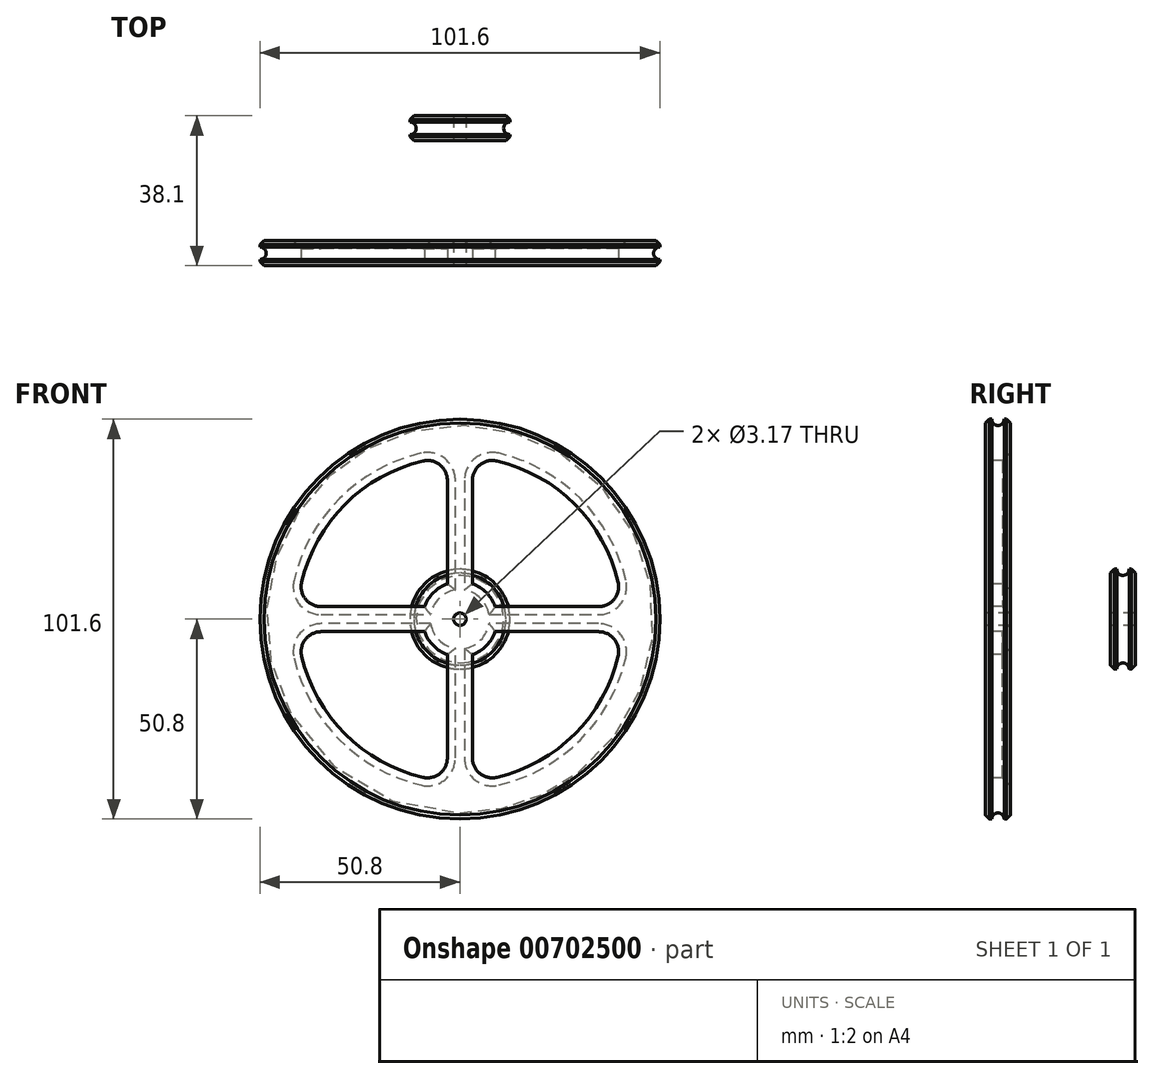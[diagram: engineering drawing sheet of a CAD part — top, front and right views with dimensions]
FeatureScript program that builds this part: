
annotation { "Feature Type Name" : "Feature", "Feature Type Description" : "" }
export const myFeature = defineFeature(function(context is Context, id is Id, definition is map)
    precondition{}
    {
        {
            var Q0;
            Q0=qCreatedBy(makeId("Right.planeOp"),FACE);
            var sketch = newSketch(context, id + "F0", { "sketchPlane" : qUnion([Q0])});
            skLineSegment(sketch, "E0", {"start": v(10.45, 0) * mm, "end": v(23.17, 0) * mm, "construction": true});
            skLineSegment(sketch, "E1", {"start": v(19.05, 1.59) * mm, "end": v(12.7, 1.59) * mm});
            skLineSegment(sketch, "E2", {"start": v(12.7, 1.59) * mm, "end": v(12.7, 12.7) * mm});
            skLineSegment(sketch, "E3", {"start": v(19.05, 1.59) * mm, "end": v(19.05, 12.7) * mm});
            skLineSegment(sketch, "E4", {"start": v(19.05, 12.7) * mm, "end": v(17.46, 12.7) * mm});
            skLineSegment(sketch, "E5", {"start": v(12.7, 12.7) * mm, "end": v(14.29, 12.7) * mm});
            skArc(sketch, "E6", {"start": v(14.29, 12.7) * mm, "mid": v(15.88, 11.11) * mm, "end": v(17.46, 12.7) * mm});
            skLineSegment(sketch, "E7", {"start": v(-12.7, 1.59) * mm, "end": v(-12.7, 50.8) * mm});
            skLineSegment(sketch, "E8", {"start": v(-12.7, 50.8) * mm, "end": v(-14.29, 50.8) * mm});
            skLineSegment(sketch, "E9", {"start": v(-12.7, 1.59) * mm, "end": v(-19.05, 1.59) * mm});
            skLineSegment(sketch, "E10", {"start": v(-19.05, 1.59) * mm, "end": v(-19.05, 50.8) * mm});
            skLineSegment(sketch, "E11", {"start": v(-19.05, 50.8) * mm, "end": v(-17.46, 50.8) * mm});
            skLineSegment(sketch, "E12", {"start": v(-3.92, 0) * mm, "end": v(-13.74, 0) * mm, "construction": true});
            skArc(sketch, "E13", {"start": v(-17.46, 50.8) * mm, "mid": v(-15.88, 49.21) * mm, "end": v(-14.29, 50.8) * mm});
            skSolve(sketch);
        }
        {
            var Q0;
            Q0=makeQuery(id+"F0.imprint","IMPRINT",FACE,{"disambiguationData":[TD([[makeQuery(id+"F0.imprint","IMPRINT",EDGE,{"derivedFrom":sQuery(id+"F0.wireOp",EDGE,"E1")}),-1.0]])]});
            var Q1;
            Q1=makeQuery(id+"F0.imprint","IMPRINT",FACE,{"disambiguationData":[TD([[makeQuery(id+"F0.imprint","IMPRINT",EDGE,{"derivedFrom":sQuery(id+"F0.wireOp",EDGE,"E7")}),1.0]])]});
            var Q2;
            Q2=sQuery(id+"F0.wireOp",EDGE,"E0");
            revolve(context, id + "F1", {"entities" : qUnion([Q0, Q1]), "axis" : qUnion([Q2]), "revolveType" : RevolveType.FULL});
        }
        {
            var Q0;
            Q0=makeQuery(id+"F1.opRevolve","SWEPT_EDGE",EDGE,{"disambiguationData":[OSD([sQuery(id+"F0.wireOp",EDGE,"E3"),sQuery(id+"F0.wireOp",EDGE,"E4")])]});
            var Q1;
            Q1=makeQuery(id+"F1.opRevolve","SWEPT_EDGE",EDGE,{"disambiguationData":[OSD([sQuery(id+"F0.wireOp",EDGE,"E2"),sQuery(id+"F0.wireOp",EDGE,"E5")])]});
            var Q2;
            Q2=makeQuery(id+"F1.opRevolve","SWEPT_EDGE",EDGE,{"disambiguationData":[OSD([sQuery(id+"F0.wireOp",EDGE,"E7"),sQuery(id+"F0.wireOp",EDGE,"E8")])]});
            var Q3;
            Q3=makeQuery(id+"F1.opRevolve","SWEPT_EDGE",EDGE,{"disambiguationData":[OSD([sQuery(id+"F0.wireOp",EDGE,"E10"),sQuery(id+"F0.wireOp",EDGE,"E11")])]});
            chamfer(context, id + "F2", {"entities" : qUnion([Q0, Q1, Q2, Q3]), "width" : 1.02 * mm, "tangentPropagation" : true});
        }
        {
            var Q0;
            Q0=makeQuery(id+"F1.opRevolve","SWEPT_FACE",FACE,{"disambiguationData":[OSD([sQuery(id+"F0.wireOp",EDGE,"E10")])]});
            var sketch = newSketch(context, id + "F3", { "sketchPlane" : qUnion([Q0])});
            skArc(sketch, "E14", {"start": v(-3.17, 8.98) * mm, "mid": v(-6.74, 6.74) * mm, "end": v(-8.98, 3.18) * mm});
            skArc(sketch, "E15", {"start": v(-3.18, 41.15) * mm, "mid": v(-29.19, 29.19) * mm, "end": v(-41.15, 3.17) * mm});
            skLineSegment(sketch, "E16", {"start": v(-3.18, 41.15) * mm, "end": v(-3.17, 8.98) * mm});
            skLineSegment(sketch, "E17", {"start": v(3.18, 41.15) * mm, "end": v(3.18, 8.98) * mm});
            skLineSegment(sketch, "E18", {"start": v(8.98, 3.18) * mm, "end": v(41.15, 3.18) * mm});
            skLineSegment(sketch, "E19", {"start": v(8.98, -3.18) * mm, "end": v(41.15, -3.18) * mm});
            skLineSegment(sketch, "E20", {"start": v(3.17, -8.98) * mm, "end": v(3.18, -41.15) * mm});
            skLineSegment(sketch, "E21", {"start": v(-3.18, -8.98) * mm, "end": v(-3.18, -41.15) * mm});
            skLineSegment(sketch, "E22", {"start": v(-8.98, -3.17) * mm, "end": v(-41.15, -3.18) * mm});
            skLineSegment(sketch, "E23", {"start": v(-8.98, 3.18) * mm, "end": v(-41.15, 3.17) * mm});
            skArc(sketch, "E24.trimOffspring", {"start": v(41.15, 3.18) * mm, "mid": v(29.19, 29.19) * mm, "end": v(3.18, 41.15) * mm});
            skArc(sketch, "E25.trimOffspring", {"start": v(3.17, -41.15) * mm, "mid": v(29.19, -29.19) * mm, "end": v(41.15, -3.18) * mm});
            skArc(sketch, "E26.trimOffspring", {"start": v(-41.15, -3.18) * mm, "mid": v(-29.19, -29.19) * mm, "end": v(-3.18, -41.15) * mm});
            skArc(sketch, "E27.trimOffspring", {"start": v(8.98, 3.18) * mm, "mid": v(6.74, 6.74) * mm, "end": v(3.18, 8.98) * mm});
            skArc(sketch, "E28.trimOffspring", {"start": v(3.17, -8.98) * mm, "mid": v(6.74, -6.74) * mm, "end": v(8.98, -3.18) * mm});
            skArc(sketch, "E29.trimOffspring", {"start": v(-8.98, -3.18) * mm, "mid": v(-6.74, -6.74) * mm, "end": v(-3.18, -8.98) * mm});
            skSolve(sketch);
        }
        {
            var Q0;
            Q0=makeQuery(id+"F3.imprint","IMPRINT",FACE,{"disambiguationData":[TD([[makeQuery(id+"F3.imprint","IMPRINT",EDGE,{"derivedFrom":sQuery(id+"F3.wireOp",EDGE,"E14")}),-1.0]])]});
            var Q1;
            Q1=makeQuery(id+"F3.imprint","IMPRINT",FACE,{"disambiguationData":[TD([[makeQuery(id+"F3.imprint","IMPRINT",EDGE,{"derivedFrom":sQuery(id+"F3.wireOp",EDGE,"E17")}),1.0]])]});
            var Q2;
            Q2=makeQuery(id+"F3.imprint","IMPRINT",FACE,{"disambiguationData":[TD([[makeQuery(id+"F3.imprint","IMPRINT",EDGE,{"derivedFrom":sQuery(id+"F3.wireOp",EDGE,"E19")}),-1.0]])]});
            var Q3;
            Q3=makeQuery(id+"F3.imprint","IMPRINT",FACE,{"disambiguationData":[TD([[makeQuery(id+"F3.imprint","IMPRINT",EDGE,{"derivedFrom":sQuery(id+"F3.wireOp",EDGE,"E21")}),-1.0]])]});
            extrude(context, id + "F4", {"entities" : qUnion([Q0, Q1, Q2, Q3]), "operationType" : NewBodyOperationType.REMOVE, "oppositeDirection" : true, "depth" : 25.4 * mm, "offsetDistance" : 25.4 * mm});
        }
        {
            var Q0;
            Q0=makeQuery(id+"F4.boolean.opBoolean","COPY",EDGE,{"derivedFrom":makeQuery(id+"F4.opExtrude","SWEPT_EDGE",EDGE,{"disambiguationData":[OSD([sQuery(id+"F3.wireOp",EDGE,"E15"),sQuery(id+"F3.wireOp",EDGE,"E16")])]})});
            var Q1;
            Q1=makeQuery(id+"F4.boolean.opBoolean","COPY",EDGE,{"derivedFrom":makeQuery(id+"F4.opExtrude","SWEPT_EDGE",EDGE,{"disambiguationData":[OSD([sQuery(id+"F3.wireOp",EDGE,"E17"),sQuery(id+"F3.wireOp",EDGE,"E24.trimOffspring")])]})});
            var Q2;
            Q2=makeQuery(id+"F4.boolean.opBoolean","COPY",EDGE,{"derivedFrom":makeQuery(id+"F4.opExtrude","SWEPT_EDGE",EDGE,{"disambiguationData":[OSD([sQuery(id+"F3.wireOp",EDGE,"E18"),sQuery(id+"F3.wireOp",EDGE,"E24.trimOffspring")])]})});
            var Q3;
            Q3=makeQuery(id+"F4.boolean.opBoolean","COPY",EDGE,{"derivedFrom":makeQuery(id+"F4.opExtrude","SWEPT_EDGE",EDGE,{"disambiguationData":[OSD([sQuery(id+"F3.wireOp",EDGE,"E19"),sQuery(id+"F3.wireOp",EDGE,"E25.trimOffspring")])]})});
            var Q4;
            Q4=makeQuery(id+"F4.boolean.opBoolean","COPY",EDGE,{"derivedFrom":makeQuery(id+"F4.opExtrude","SWEPT_EDGE",EDGE,{"disambiguationData":[OSD([sQuery(id+"F3.wireOp",EDGE,"E20"),sQuery(id+"F3.wireOp",EDGE,"E25.trimOffspring")])]})});
            var Q5;
            Q5=makeQuery(id+"F4.boolean.opBoolean","COPY",EDGE,{"derivedFrom":makeQuery(id+"F4.opExtrude","SWEPT_EDGE",EDGE,{"disambiguationData":[OSD([sQuery(id+"F3.wireOp",EDGE,"E21"),sQuery(id+"F3.wireOp",EDGE,"E26.trimOffspring")])]})});
            var Q6;
            Q6=makeQuery(id+"F4.boolean.opBoolean","COPY",EDGE,{"derivedFrom":makeQuery(id+"F4.opExtrude","SWEPT_EDGE",EDGE,{"disambiguationData":[OSD([sQuery(id+"F3.wireOp",EDGE,"E22"),sQuery(id+"F3.wireOp",EDGE,"E26.trimOffspring")])]})});
            var Q7;
            Q7=makeQuery(id+"F4.boolean.opBoolean","COPY",EDGE,{"derivedFrom":makeQuery(id+"F4.opExtrude","SWEPT_EDGE",EDGE,{"disambiguationData":[OSD([sQuery(id+"F3.wireOp",EDGE,"E15"),sQuery(id+"F3.wireOp",EDGE,"E23")])]})});
            fillet(context, id + "F5", {"entities" : qUnion([Q0, Q1, Q2, Q3, Q4, Q5, Q6, Q7]), "radius" : 5.08 * mm, "tangentPropagation" : true, "allowEdgeOverflow" : false});
        }
        {
            var Q0;
            Q0=makeQuery(id+"F4.boolean.opBoolean","COPY",EDGE,{"derivedFrom":makeQuery(id+"F4.opExtrude","CAP_EDGE",EDGE,{"disambiguationData":[OSD([sQuery(id+"F3.wireOp",EDGE,"E22")])],"isStart":true})});
            var Q1;
            Q1=makeQuery(id+"F4.boolean.opBoolean","COPY",EDGE,{"derivedFrom":makeQuery(id+"F4.opExtrude","CAP_EDGE",EDGE,{"disambiguationData":[OSD([sQuery(id+"F3.wireOp",EDGE,"E15")])],"isStart":true})});
            var Q2;
            Q2=makeQuery(id+"F4.boolean.opBoolean","COPY",EDGE,{"derivedFrom":makeQuery(id+"F4.opExtrude","CAP_EDGE",EDGE,{"disambiguationData":[OSD([sQuery(id+"F3.wireOp",EDGE,"E24.trimOffspring")])],"isStart":true})});
            var Q3;
            Q3=makeQuery(id+"F4.boolean.opBoolean","COPY",EDGE,{"derivedFrom":makeQuery(id+"F4.opExtrude","CAP_EDGE",EDGE,{"disambiguationData":[OSD([sQuery(id+"F3.wireOp",EDGE,"E25.trimOffspring")])],"isStart":true})});
            var Q4;
            Q4=makeQuery(id+"F4.boolean.opBoolean","INTERSECT",EDGE,{"derivedFrom":[makeQuery(id+"F1.opRevolve","SWEPT_FACE",FACE,{"disambiguationData":[OSD([sQuery(id+"F0.wireOp",EDGE,"E7")])]}),makeQuery(id+"F4.opExtrude","SWEPT_FACE",FACE,{"disambiguationData":[OSD([sQuery(id+"F3.wireOp",EDGE,"E19")])]})]});
            var Q5;
            Q5=makeQuery(id+"F4.boolean.opBoolean","INTERSECT",EDGE,{"derivedFrom":[makeQuery(id+"F1.opRevolve","SWEPT_FACE",FACE,{"disambiguationData":[OSD([sQuery(id+"F0.wireOp",EDGE,"E7")])]}),makeQuery(id+"F4.opExtrude","SWEPT_FACE",FACE,{"disambiguationData":[OSD([sQuery(id+"F3.wireOp",EDGE,"E18")])]})]});
            var Q6;
            Q6=makeQuery(id+"F4.boolean.opBoolean","INTERSECT",EDGE,{"derivedFrom":[makeQuery(id+"F1.opRevolve","SWEPT_FACE",FACE,{"disambiguationData":[OSD([sQuery(id+"F0.wireOp",EDGE,"E7")])]}),makeQuery(id+"F4.opExtrude","SWEPT_FACE",FACE,{"disambiguationData":[OSD([sQuery(id+"F3.wireOp",EDGE,"E15")])]})]});
            var Q7;
            Q7=makeQuery(id+"F4.boolean.opBoolean","INTERSECT",EDGE,{"derivedFrom":[makeQuery(id+"F1.opRevolve","SWEPT_FACE",FACE,{"disambiguationData":[OSD([sQuery(id+"F0.wireOp",EDGE,"E7")])]}),makeQuery(id+"F4.opExtrude","SWEPT_FACE",FACE,{"disambiguationData":[OSD([sQuery(id+"F3.wireOp",EDGE,"E22")])]})]});
            var Q8;
            Q8=makeQuery(id+"F4.boolean.opBoolean","INTERSECT",EDGE,{"derivedFrom":[makeQuery(id+"F1.opRevolve","SWEPT_FACE",FACE,{"disambiguationData":[OSD([sQuery(id+"F0.wireOp",EDGE,"E7")])]}),makeQuery(id+"F4.opExtrude","SWEPT_FACE",FACE,{"disambiguationData":[OSD([sQuery(id+"F3.wireOp",EDGE,"E14")])]})]});
            var Q9;
            Q9=makeQuery(id+"F4.boolean.opBoolean","INTERSECT",EDGE,{"derivedFrom":[makeQuery(id+"F1.opRevolve","SWEPT_FACE",FACE,{"disambiguationData":[OSD([sQuery(id+"F0.wireOp",EDGE,"E7")])]}),makeQuery(id+"F4.opExtrude","SWEPT_FACE",FACE,{"disambiguationData":[OSD([sQuery(id+"F3.wireOp",EDGE,"E27.trimOffspring")])]})]});
            var Q10;
            Q10=makeQuery(id+"F4.boolean.opBoolean","INTERSECT",EDGE,{"derivedFrom":[makeQuery(id+"F1.opRevolve","SWEPT_FACE",FACE,{"disambiguationData":[OSD([sQuery(id+"F0.wireOp",EDGE,"E7")])]}),makeQuery(id+"F4.opExtrude","SWEPT_FACE",FACE,{"disambiguationData":[OSD([sQuery(id+"F3.wireOp",EDGE,"E28.trimOffspring")])]})]});
            var Q11;
            Q11=makeQuery(id+"F4.boolean.opBoolean","INTERSECT",EDGE,{"derivedFrom":[makeQuery(id+"F1.opRevolve","SWEPT_FACE",FACE,{"disambiguationData":[OSD([sQuery(id+"F0.wireOp",EDGE,"E7")])]}),makeQuery(id+"F4.opExtrude","SWEPT_FACE",FACE,{"disambiguationData":[OSD([sQuery(id+"F3.wireOp",EDGE,"E29.trimOffspring")])]})]});
            var Q12;
            Q12=makeQuery(id+"F4.boolean.opBoolean","COPY",EDGE,{"derivedFrom":makeQuery(id+"F4.opExtrude","CAP_EDGE",EDGE,{"disambiguationData":[OSD([sQuery(id+"F3.wireOp",EDGE,"E27.trimOffspring")])],"isStart":true})});
            var Q13;
            Q13=makeQuery(id+"F4.boolean.opBoolean","COPY",EDGE,{"derivedFrom":makeQuery(id+"F4.opExtrude","CAP_EDGE",EDGE,{"disambiguationData":[OSD([sQuery(id+"F3.wireOp",EDGE,"E14")])],"isStart":true})});
            var Q14;
            Q14=makeQuery(id+"F4.boolean.opBoolean","COPY",EDGE,{"derivedFrom":makeQuery(id+"F4.opExtrude","CAP_EDGE",EDGE,{"disambiguationData":[OSD([sQuery(id+"F3.wireOp",EDGE,"E29.trimOffspring")])],"isStart":true})});
            var Q15;
            Q15=makeQuery(id+"F4.boolean.opBoolean","COPY",EDGE,{"derivedFrom":makeQuery(id+"F4.opExtrude","CAP_EDGE",EDGE,{"disambiguationData":[OSD([sQuery(id+"F3.wireOp",EDGE,"E28.trimOffspring")])],"isStart":true})});
            chamfer(context, id + "F6", {"entities" : qUnion([Q0, Q1, Q2, Q3, Q4, Q5, Q6, Q7, Q8, Q9, Q10, Q11, Q12, Q13, Q14, Q15]), "width" : 2.03 * mm, "tangentPropagation" : true});
        }
    });
